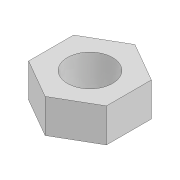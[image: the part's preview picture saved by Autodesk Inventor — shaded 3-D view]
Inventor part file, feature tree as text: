
AUTODESK INVENTOR PART (.ipt)
format: ipt  version: 2022 (Build 260153000, 153)  size: 84,992 bytes
history: native  units: mm
features: extrude x1, sketch x1
ambient origin geometry x8: Origin, YZ Plane, XZ Plane, XY Plane, X Axis, Y Axis, Z Axis, Center Point
bodies: Solid1 (feature_tree)
feature tree (2):
  extrude  "Extrusion1"  Depth=3.0mm
  sketch  "Sketch1"  dims[d0=6.9mm d1=4.0mm d2=3.0mm d3=0.0mm]
